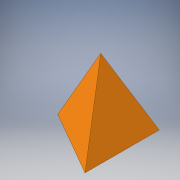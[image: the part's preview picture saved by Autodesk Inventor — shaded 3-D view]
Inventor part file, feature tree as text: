
AUTODESK INVENTOR PART (.ipt)
format: ipt  version: 2019 (Build 230136000, 136)  size: 107,008 bytes
history: native  units: in
note: dims shown in document units (in); Inventor stores cm internally (conversion verified against a paired STEP export)
features: sketch x3, plane x1, loft x1, hole x1
ambient origin geometry x8: Origin, YZ Plane, XZ Plane, XY Plane, X Axis, Y Axis, Z Axis, Center Point
bodies: Solid1 (feature_tree)
feature tree (6):
  sketch  "Sketch1"  dims[d0=2.0in d1=4.0in]
  plane  "Work Plane1"
  loft  "Loft1"
  hole  "Hole1"  [1 undecoded]
  sketch  "Sketch2"  dims[d2=3.464in d3=4.0in]
  sketch  "Sketch3"  dims[d6=0.0in d7=90.0deg d8=0.0in d9=90.0deg d13=0.3in d14=0.75in d15=0.375in d16=0.25in d17=0.5635in d18=2.0in d19=0.0in d20=0.75in d21=0.8108in d22=0.0625in d23=0.75in d24=0.375in]
note: 1 required parameter value undecoded (feature->parameter linkage not recoverable at this tier; creation-order binding heuristic only, values carry confidence <= 0.55)
